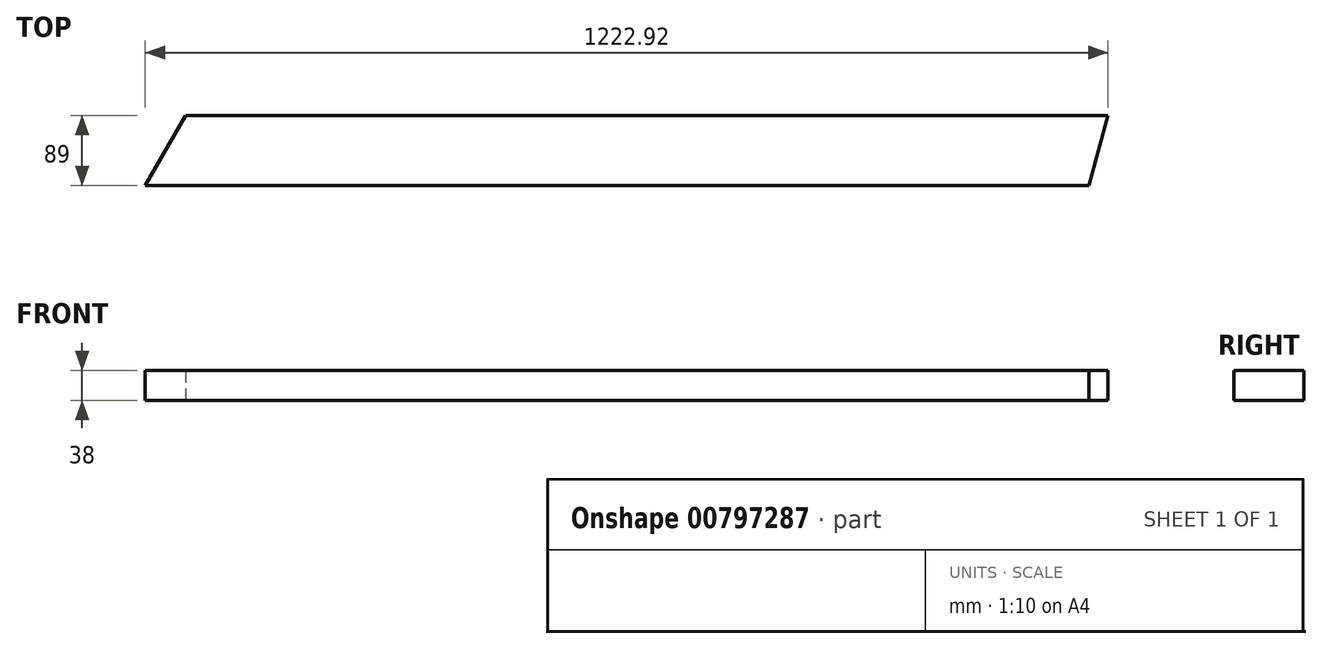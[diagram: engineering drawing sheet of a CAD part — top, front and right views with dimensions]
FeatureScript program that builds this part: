
annotation { "Feature Type Name" : "Feature", "Feature Type Description" : "" }
export const myFeature = defineFeature(function(context is Context, id is Id, definition is map)
    precondition{}
    {
        {
            var Q0;
            Q0=qCreatedBy(makeId("Top.planeOp"),FACE);
            var sketch = newSketch(context, id + "F0", { "sketchPlane" : qUnion([Q0])});
            skLineSegment(sketch, "E0.bottom", {"start": v(472.92, 44.5) * mm, "end": v(-698.62, 44.5) * mm});
            skLineSegment(sketch, "E0.top", {"start": v(449.07, -44.5) * mm, "end": v(-750, -44.5) * mm});
            skPoint(sketch, "E0.middle", {"position": v(0, 0) * mm});
            skLineSegment(sketch, "E1", {"start": v(449.07, -44.5) * mm, "end": v(472.92, 44.5) * mm});
            skLineSegment(sketch, "E2", {"start": v(-750, -44.5) * mm, "end": v(-698.62, 44.5) * mm});
            skPoint(sketch, "E0.left.start.orphan", {"position": v(750, 44.5) * mm});
            skPoint(sketch, "E0.right.start.orphan", {"position": v(-449.07, 44.5) * mm});
            skSolve(sketch);
        }
        {
            var Q0;
            Q0 = qSketchRegion(id + "F0", true);
            extrude(context, id + "F1", {"entities" : qUnion([Q0]), "depth" : 38 * mm, "offsetDistance" : 25 * mm, "symmetric" : true});
        }
    });
